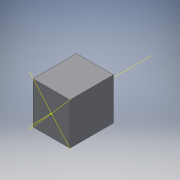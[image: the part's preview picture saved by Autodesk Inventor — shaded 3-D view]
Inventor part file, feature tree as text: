
AUTODESK INVENTOR PART (.ipt)
format: ipt  version: 2017 (Build 210142000, 142)  size: 98,304 bytes
history: native  units: in
note: dims shown in document units (in); Inventor stores cm internally (conversion verified against a paired STEP export)
features: other x8, sketch x2, extrude x1, plane x1
ambient origin geometry x8: Origin, YZ Plane, XZ Plane, XY Plane, X Axis, Y Axis, Z Axis, Center Point
bodies: Solid1 (feature_tree)
feature tree (12):
  extrude  "Extrusion1"  Depth=0.8661in
  other  "Work Point1"
  other  "Work Point2"
  other  "Work Point3"
  other  "Work Point4"
  plane  "Work Plane1"
  sketch  "Sketch5"  dims[d2=0.9843in d3=0.0in d9=90.0deg]
  sketch  "Sketch2"  dims[d0=1.0236in d1=0.8661in]
  other  "Work Axis1"
  other  "Work Axis2"
  other  "Work Point5"
  other  "Work Axis3"
